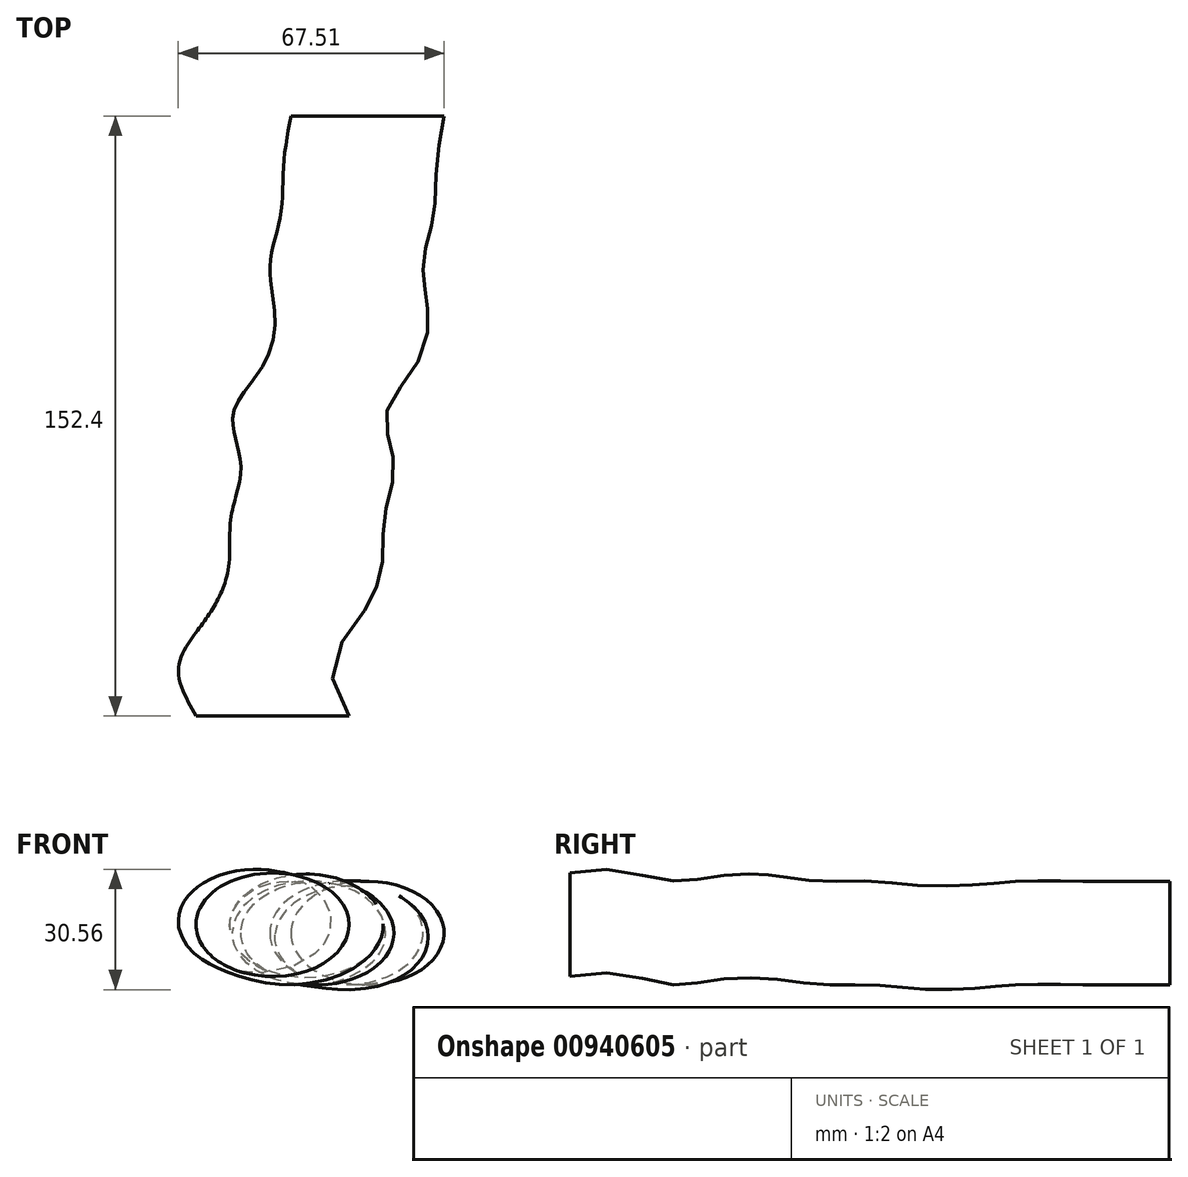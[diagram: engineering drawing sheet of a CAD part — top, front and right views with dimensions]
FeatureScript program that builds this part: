
annotation { "Feature Type Name" : "Feature", "Feature Type Description" : "" }
export const myFeature = defineFeature(function(context is Context, id is Id, definition is map)
    precondition{}
    {
        {
            var Q0;
            Q0=qCreatedBy(makeId("Front.planeOp"),FACE);
            cPlane(context, id + "F0", {"entities" : qUnion([Q0]), "cplaneType" : CPlaneType.OFFSET, "offset" : 12.7 * mm, "width" : 152.4 * mm, "height" : 152.4 * mm});
        }
        {
            var Q0;
            Q0=qCreatedBy(id+"F0.planeOp",FACE);
            cPlane(context, id + "F1", {"entities" : qUnion([Q0]), "cplaneType" : CPlaneType.OFFSET, "offset" : 25.4 * mm, "width" : 152.4 * mm, "height" : 152.4 * mm});
        }
        {
            var Q0;
            Q0=qCreatedBy(id+"F1.planeOp",FACE);
            cPlane(context, id + "F2", {"entities" : qUnion([Q0]), "cplaneType" : CPlaneType.OFFSET, "offset" : 25.4 * mm, "width" : 152.4 * mm, "height" : 152.4 * mm});
        }
        {
            var Q0;
            Q0=qCreatedBy(id+"F2.planeOp",FACE);
            cPlane(context, id + "F3", {"entities" : qUnion([Q0]), "cplaneType" : CPlaneType.OFFSET, "offset" : 12.7 * mm, "width" : 152.4 * mm, "height" : 152.4 * mm});
        }
        {
            var Q0;
            Q0=qCreatedBy(id+"F1.planeOp",FACE);
            cPlane(context, id + "F4", {"entities" : qUnion([Q0]), "cplaneType" : CPlaneType.OFFSET, "offset" : 12.7 * mm, "width" : 152.4 * mm, "height" : 152.4 * mm});
        }
        {
            var Q0;
            Q0=qCreatedBy(id+"F0.planeOp",FACE);
            cPlane(context, id + "F5", {"entities" : qUnion([Q0]), "cplaneType" : CPlaneType.OFFSET, "offset" : 12.7 * mm, "width" : 152.4 * mm, "height" : 152.4 * mm});
        }
        {
            var Q0;
            Q0=qCreatedBy(makeId("Front.planeOp"),FACE);
            cPlane(context, id + "F6", {"entities" : qUnion([Q0]), "cplaneType" : CPlaneType.OFFSET, "offset" : 12.7 * mm, "oppositeDirection" : true, "width" : 152.4 * mm, "height" : 152.4 * mm});
        }
        {
            var Q0;
            Q0=qCreatedBy(id+"F6.planeOp",FACE);
            cPlane(context, id + "F7", {"entities" : qUnion([Q0]), "cplaneType" : CPlaneType.OFFSET, "offset" : 12.7 * mm, "oppositeDirection" : true, "width" : 152.4 * mm, "height" : 152.4 * mm});
        }
        {
            var Q0;
            Q0=qCreatedBy(id+"F7.planeOp",FACE);
            cPlane(context, id + "F8", {"entities" : qUnion([Q0]), "cplaneType" : CPlaneType.OFFSET, "offset" : 12.7 * mm, "oppositeDirection" : true, "width" : 152.4 * mm, "height" : 152.4 * mm});
        }
        {
            var Q0;
            Q0=qCreatedBy(id+"F8.planeOp",FACE);
            cPlane(context, id + "F9", {"entities" : qUnion([Q0]), "cplaneType" : CPlaneType.OFFSET, "offset" : 25.4 * mm, "oppositeDirection" : true, "width" : 152.4 * mm, "height" : 152.4 * mm});
        }
        {
            var Q0;
            Q0=qCreatedBy(id+"F9.planeOp",FACE);
            cPlane(context, id + "F10", {"entities" : qUnion([Q0]), "cplaneType" : CPlaneType.OFFSET, "offset" : 12.7 * mm, "oppositeDirection" : true, "width" : 152.4 * mm, "height" : 152.4 * mm});
        }
        {
            var Q0;
            Q0=qCreatedBy(id+"F9.planeOp",FACE);
            cPlane(context, id + "F11", {"entities" : qUnion([Q0]), "cplaneType" : CPlaneType.OFFSET, "offset" : 12.7 * mm, "width" : 152.4 * mm, "height" : 152.4 * mm});
        }
        {
            var Q0;
            Q0=qCreatedBy(makeId("Top.planeOp"),FACE);
            cPlane(context, id + "F12", {"entities" : qUnion([Q0]), "cplaneType" : CPlaneType.OFFSET, "offset" : 25.4 * mm, "width" : 152.4 * mm, "height" : 152.4 * mm});
        }
        {
            var Q0;
            Q0=qCreatedBy(id+"F12.planeOp",FACE);
            cPlane(context, id + "F13", {"entities" : qUnion([Q0]), "cplaneType" : CPlaneType.OFFSET, "offset" : 25.4 * mm, "width" : 152.4 * mm, "height" : 152.4 * mm});
        }
        {
            var Q0;
            Q0=qCreatedBy(makeId("Top.planeOp"),FACE);
            cPlane(context, id + "F14", {"entities" : qUnion([Q0]), "cplaneType" : CPlaneType.OFFSET, "offset" : 25.4 * mm, "oppositeDirection" : true, "width" : 152.4 * mm, "height" : 152.4 * mm});
        }
        {
            var Q0;
            Q0=qCreatedBy(id+"F14.planeOp",FACE);
            cPlane(context, id + "F15", {"entities" : qUnion([Q0]), "cplaneType" : CPlaneType.OFFSET, "offset" : 25.4 * mm, "oppositeDirection" : true, "width" : 152.4 * mm, "height" : 152.4 * mm});
        }
        {
            var Q0;
            Q0=qCreatedBy(id+"F3.planeOp",FACE);
            var sketch = newSketch(context, id + "F16", { "sketchPlane" : qUnion([Q0])});
            skEllipse(sketch, "E0", {"center": v(0, 2.08) * mm, "majorRadius": 19.45 * mm, "minorRadius": 13.15 * mm, "majorAxis": v(-1, 0)});
            skSolve(sketch);
        }
        {
            var Q0;
            Q0=qCreatedBy(id+"F2.planeOp",FACE);
            var sketch = newSketch(context, id + "F17", { "sketchPlane" : qUnion([Q0])});
            skEllipse(sketch, "E1", {"center": v(-4.4, 2.8) * mm, "majorRadius": 19.45 * mm, "minorRadius": 13.15 * mm, "majorAxis": v(-1, 0)});
            skSolve(sketch);
        }
        {
            var Q0;
            Q0=qCreatedBy(id+"F4.planeOp",FACE);
            var sketch = newSketch(context, id + "F18", { "sketchPlane" : qUnion([Q0])});
            skEllipse(sketch, "E2", {"center": v(3.05, 0.06) * mm, "majorRadius": 19.45 * mm, "minorRadius": 13.15 * mm, "majorAxis": v(-1, 0)});
            skSolve(sketch);
        }
        {
            var Q0;
            Q0=qCreatedBy(id+"F1.planeOp",FACE);
            var sketch = newSketch(context, id + "F19", { "sketchPlane" : qUnion([Q0])});
            skEllipse(sketch, "E3", {"center": v(8.34, 1.35) * mm, "majorRadius": 19.45 * mm, "minorRadius": 13.15 * mm, "majorAxis": v(-1, 0)});
            skSolve(sketch);
        }
        {
            var Q0;
            Q0=qCreatedBy(id+"F5.planeOp",FACE);
            var sketch = newSketch(context, id + "F20", { "sketchPlane" : qUnion([Q0])});
            skEllipse(sketch, "E4", {"center": v(8.95, 1.52) * mm, "majorRadius": 19.45 * mm, "minorRadius": 13.15 * mm, "majorAxis": v(-1, 0)});
            skSolve(sketch);
        }
        {
            var Q0;
            Q0=qCreatedBy(id+"F0.planeOp",FACE);
            var sketch = newSketch(context, id + "F21", { "sketchPlane" : qUnion([Q0])});
            skEllipse(sketch, "E5", {"center": v(11.41, 0) * mm, "majorRadius": 19.45 * mm, "minorRadius": 13.15 * mm, "majorAxis": v(-1, 0)});
            skSolve(sketch);
        }
        {
            var Q0;
            Q0=qCreatedBy(makeId("Front.planeOp"),FACE);
            var sketch = newSketch(context, id + "F22", { "sketchPlane" : qUnion([Q0])});
            skEllipse(sketch, "E6", {"center": v(9.38, 0) * mm, "majorRadius": 19.45 * mm, "minorRadius": 13.15 * mm, "majorAxis": v(-1, 0)});
            skSolve(sketch);
        }
        {
            var Q0;
            Q0=qCreatedBy(id+"F6.planeOp",FACE);
            var sketch = newSketch(context, id + "F23", { "sketchPlane" : qUnion([Q0])});
            skEllipse(sketch, "E7", {"center": v(16.97, -1.09) * mm, "majorRadius": 19.45 * mm, "minorRadius": 13.15 * mm, "majorAxis": v(-1, 0)});
            skSolve(sketch);
        }
        {
            var Q0;
            Q0=qCreatedBy(id+"F7.planeOp",FACE);
            var sketch = newSketch(context, id + "F24", { "sketchPlane" : qUnion([Q0])});
            skEllipse(sketch, "E8", {"center": v(20.1, -1) * mm, "majorRadius": 19.45 * mm, "minorRadius": 13.15 * mm, "majorAxis": v(-1, 0)});
            skSolve(sketch);
        }
        {
            var Q0;
            Q0=qCreatedBy(id+"F8.planeOp",FACE);
            var sketch = newSketch(context, id + "F25", { "sketchPlane" : qUnion([Q0])});
            skEllipse(sketch, "E9", {"center": v(18.8, 0) * mm, "majorRadius": 19.45 * mm, "minorRadius": 13.15 * mm, "majorAxis": v(-1, 0)});
            skSolve(sketch);
        }
        {
            var Q0;
            Q0=qCreatedBy(id+"F11.planeOp",FACE);
            var sketch = newSketch(context, id + "F26", { "sketchPlane" : qUnion([Q0])});
            skEllipse(sketch, "E10", {"center": v(21.46, 0) * mm, "majorRadius": 19.45 * mm, "minorRadius": 13.15 * mm, "majorAxis": v(-1, 0)});
            skSolve(sketch);
        }
        {
            var Q0;
            Q0=qCreatedBy(id+"F9.planeOp",FACE);
            var sketch = newSketch(context, id + "F27", { "sketchPlane" : qUnion([Q0])});
            skEllipse(sketch, "E11", {"center": v(22.24, 0) * mm, "majorRadius": 19.45 * mm, "minorRadius": 13.15 * mm, "majorAxis": v(-1, 0)});
            skSolve(sketch);
        }
        {
            var Q0;
            Q0=qCreatedBy(id+"F10.planeOp",FACE);
            var sketch = newSketch(context, id + "F28", { "sketchPlane" : qUnion([Q0])});
            skEllipse(sketch, "E12", {"center": v(24.13, 0) * mm, "majorRadius": 19.45 * mm, "minorRadius": 13.15 * mm, "majorAxis": v(-1, 0)});
            skSolve(sketch);
        }
        {
            var Q0;
            Q0=makeQuery(id+"F16.imprint","IMPRINT",FACE,{"disambiguationData":[TD([[makeQuery(id+"F16.imprint","IMPRINT",EDGE,{"derivedFrom":sQuery(id+"F16.wireOp",EDGE,"E0")}),1.0]])]});
            var Q1;
            Q1=makeQuery(id+"F17.imprint","IMPRINT",FACE,{"disambiguationData":[TD([[makeQuery(id+"F17.imprint","IMPRINT",EDGE,{"derivedFrom":sQuery(id+"F17.wireOp",EDGE,"E1")}),1.0]])]});
            var Q2;
            Q2=makeQuery(id+"F18.imprint","IMPRINT",FACE,{"disambiguationData":[TD([[makeQuery(id+"F18.imprint","IMPRINT",EDGE,{"derivedFrom":sQuery(id+"F18.wireOp",EDGE,"E2")}),1.0]])]});
            var Q3;
            Q3=makeQuery(id+"F19.imprint","IMPRINT",FACE,{"disambiguationData":[TD([[makeQuery(id+"F19.imprint","IMPRINT",EDGE,{"derivedFrom":sQuery(id+"F19.wireOp",EDGE,"E3")}),1.0]])]});
            var Q4;
            Q4=makeQuery(id+"F20.imprint","IMPRINT",FACE,{"disambiguationData":[TD([[makeQuery(id+"F20.imprint","IMPRINT",EDGE,{"derivedFrom":sQuery(id+"F20.wireOp",EDGE,"E4")}),1.0]])]});
            var Q5;
            Q5=makeQuery(id+"F21.imprint","IMPRINT",FACE,{"disambiguationData":[TD([[makeQuery(id+"F21.imprint","IMPRINT",EDGE,{"derivedFrom":sQuery(id+"F21.wireOp",EDGE,"E5")}),1.0]])]});
            var Q6;
            Q6=makeQuery(id+"F22.imprint","IMPRINT",FACE,{"disambiguationData":[TD([[makeQuery(id+"F22.imprint","IMPRINT",EDGE,{"derivedFrom":sQuery(id+"F22.wireOp",EDGE,"E6")}),1.0]])]});
            var Q7;
            Q7=makeQuery(id+"F23.imprint","IMPRINT",FACE,{"disambiguationData":[TD([[makeQuery(id+"F23.imprint","IMPRINT",EDGE,{"derivedFrom":sQuery(id+"F23.wireOp",EDGE,"E7")}),1.0]])]});
            var Q8;
            Q8=makeQuery(id+"F24.imprint","IMPRINT",FACE,{"disambiguationData":[TD([[makeQuery(id+"F24.imprint","IMPRINT",EDGE,{"derivedFrom":sQuery(id+"F24.wireOp",EDGE,"E8")}),1.0]])]});
            var Q9;
            Q9=makeQuery(id+"F25.imprint","IMPRINT",FACE,{"disambiguationData":[TD([[makeQuery(id+"F25.imprint","IMPRINT",EDGE,{"derivedFrom":sQuery(id+"F25.wireOp",EDGE,"E9")}),1.0]])]});
            var Q10;
            Q10=makeQuery(id+"F26.imprint","IMPRINT",FACE,{"disambiguationData":[TD([[makeQuery(id+"F26.imprint","IMPRINT",EDGE,{"derivedFrom":sQuery(id+"F26.wireOp",EDGE,"E10")}),1.0]])]});
            var Q11;
            Q11=makeQuery(id+"F27.imprint","IMPRINT",FACE,{"disambiguationData":[TD([[makeQuery(id+"F27.imprint","IMPRINT",EDGE,{"derivedFrom":sQuery(id+"F27.wireOp",EDGE,"E11")}),1.0]])]});
            var Q12;
            Q12=makeQuery(id+"F28.imprint","IMPRINT",FACE,{"disambiguationData":[TD([[makeQuery(id+"F28.imprint","IMPRINT",EDGE,{"derivedFrom":sQuery(id+"F28.wireOp",EDGE,"E12")}),1.0]])]});
            loft(context, id + "F29", {"sheetProfilesArray" : [{ "sheetProfileEntities" : qUnion([Q0]) }, { "sheetProfileEntities" : qUnion([Q1]) }, { "sheetProfileEntities" : qUnion([Q2]) }, { "sheetProfileEntities" : qUnion([Q3]) }, { "sheetProfileEntities" : qUnion([Q4]) }, { "sheetProfileEntities" : qUnion([Q5]) }, { "sheetProfileEntities" : qUnion([Q6]) }, { "sheetProfileEntities" : qUnion([Q7]) }, { "sheetProfileEntities" : qUnion([Q8]) }, { "sheetProfileEntities" : qUnion([Q9]) }, { "sheetProfileEntities" : qUnion([Q10]) }, { "sheetProfileEntities" : qUnion([Q11]) }, { "sheetProfileEntities" : qUnion([Q12]) }]});
        }
    });
